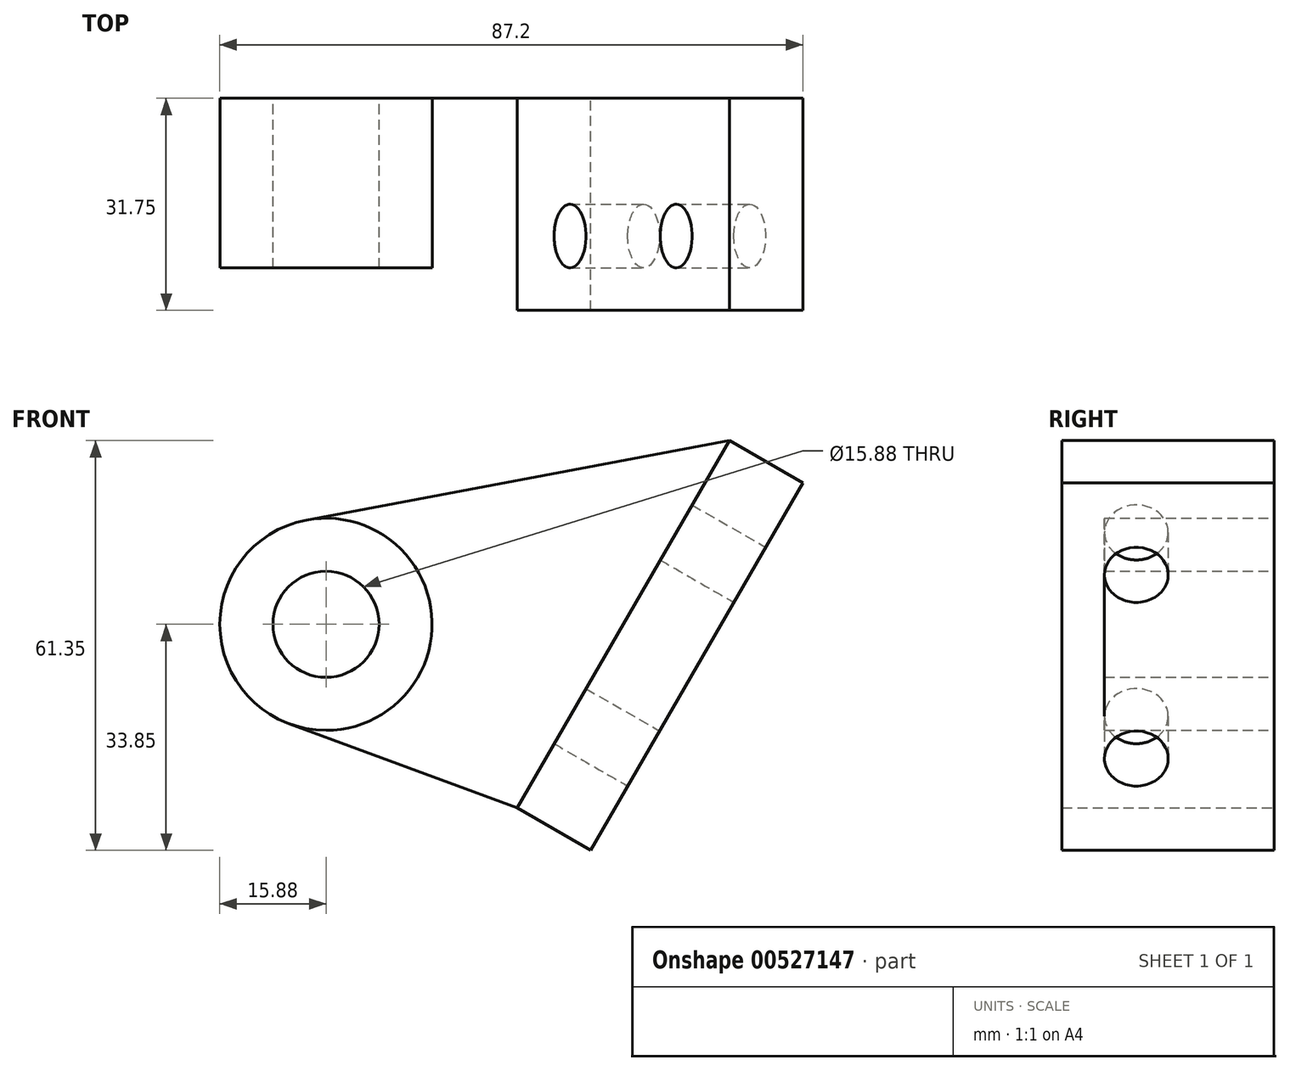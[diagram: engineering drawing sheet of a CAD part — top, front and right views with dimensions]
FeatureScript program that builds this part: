
annotation { "Feature Type Name" : "Feature", "Feature Type Description" : "" }
export const myFeature = defineFeature(function(context is Context, id is Id, definition is map)
    precondition{}
    {
        {
            var Q0;
            Q0=qCreatedBy(makeId("Front.planeOp"),FACE);
            var sketch = newSketch(context, id + "F0", { "sketchPlane" : qUnion([Q0])});
            skLineSegment(sketch, "E0", {"start": v(0, 64.1) * mm, "end": v(0, -64.1) * mm, "construction": true});
            skPoint(sketch, "E1", {"position": v(0, 0) * mm});
            skLineSegment(sketch, "E2", {"start": v(-130.85, 0) * mm, "end": v(130.85, 0) * mm, "construction": true});
            skCircle(sketch, "E3", {"center": v(0, 0) * mm, "radius": 7.94 * mm});
            skCircle(sketch, "E4", {"center": v(0, 0) * mm, "radius": 15.88 * mm});
            skLineSegment(sketch, "E5", {"start": v(44.45, 58.65) * mm, "end": v(44.45, -58.65) * mm, "construction": true});
            skPoint(sketch, "E6", {"position": v(44.45, 0) * mm});
            skLineSegment(sketch, "E7", {"start": v(60.33, 27.5) * mm, "end": v(28.57, -27.5) * mm});
            skLineSegment(sketch, "E8.0", {"start": v(71.32, 21.15) * mm, "end": v(39.57, -33.85) * mm});
            skLineSegment(sketch, "E9", {"start": v(60.33, 27.5) * mm, "end": v(71.32, 21.15) * mm});
            skLineSegment(sketch, "E10", {"start": v(28.57, -27.5) * mm, "end": v(39.57, -33.85) * mm});
            skLineSegment(sketch, "E11", {"start": v(60.33, 27.5) * mm, "end": v(-2.93, 15.6) * mm});
            skLineSegment(sketch, "E12", {"start": v(28.58, -27.5) * mm, "end": v(-5.5, -14.89) * mm});
            skSolve(sketch);
        }
        {
            var Q0;
            Q0=makeQuery(id+"F0.imprint","IMPRINT",FACE,{"disambiguationData":[TD([[makeQuery(id+"F0.imprint","IMPRINT",EDGE,{"derivedFrom":sQuery(id+"F0.wireOp",EDGE,"E7")}),-1.0]])]});
            extrude(context, id + "F1", {"entities" : qUnion([Q0]), "depth" : 3 / 203.2 * mm, "offsetDistance" : 25.4 * mm});
        }
        {
            var Q0;
            Q0=makeQuery(id+"F0.imprint","IMPRINT",FACE,{"disambiguationData":[TD([[makeQuery(id+"F0.imprint","IMPRINT",EDGE,{"derivedFrom":sQuery(id+"F0.wireOp",EDGE,"E3")}),-1.0]])]});
            extrude(context, id + "F2", {"entities" : qUnion([Q0]), "operationType" : NewBodyOperationType.ADD, "depth" : 25.4 * mm, "offsetDistance" : 25.4 * mm});
        }
        {
            var Q0;
            Q0=makeQuery(id+"F0.imprint","IMPRINT",FACE,{"disambiguationData":[TD([[makeQuery(id+"F0.imprint","IMPRINT",EDGE,{"derivedFrom":sQuery(id+"F0.wireOp",EDGE,"E7")}),1.0]])]});
            extrude(context, id + "F3", {"entities" : qUnion([Q0]), "operationType" : NewBodyOperationType.ADD, "depth" : 31.75 * mm, "offsetDistance" : 25.4 * mm});
        }
        {
            var Q0;
            Q0=makeQuery(id+"F3.opExtrude","SWEPT_FACE",FACE,{"disambiguationData":[OSD([sQuery(id+"F0.wireOp",EDGE,"E8.0")])]});
            var sketch = newSketch(context, id + "F4", { "sketchPlane" : qUnion([Q0])});
            skCircle(sketch, "E13", {"center": v(-20.64, 6.35) * mm, "radius": 4.76 * mm});
            skCircle(sketch, "E14", {"center": v(-20.64, 38.1) * mm, "radius": 4.76 * mm});
            skSolve(sketch);
        }
        {
            var Q0;
            Q0=makeQuery(id+"F4.imprint","IMPRINT",FACE,{"disambiguationData":[TD([[makeQuery(id+"F4.imprint","IMPRINT",EDGE,{"derivedFrom":sQuery(id+"F4.wireOp",EDGE,"E13")}),1.0]])]});
            var Q1;
            Q1=makeQuery(id+"F4.imprint","IMPRINT",FACE,{"disambiguationData":[TD([[makeQuery(id+"F4.imprint","IMPRINT",EDGE,{"derivedFrom":sQuery(id+"F4.wireOp",EDGE,"E14")}),1.0]])]});
            extrude(context, id + "F5", {"entities" : qUnion([Q0, Q1]), "operationType" : NewBodyOperationType.REMOVE, "endBound" : BoundingType.UP_TO_NEXT, "oppositeDirection" : true, "depth" : 25.4 * mm, "offsetDistance" : 25.4 * mm});
        }
    });
